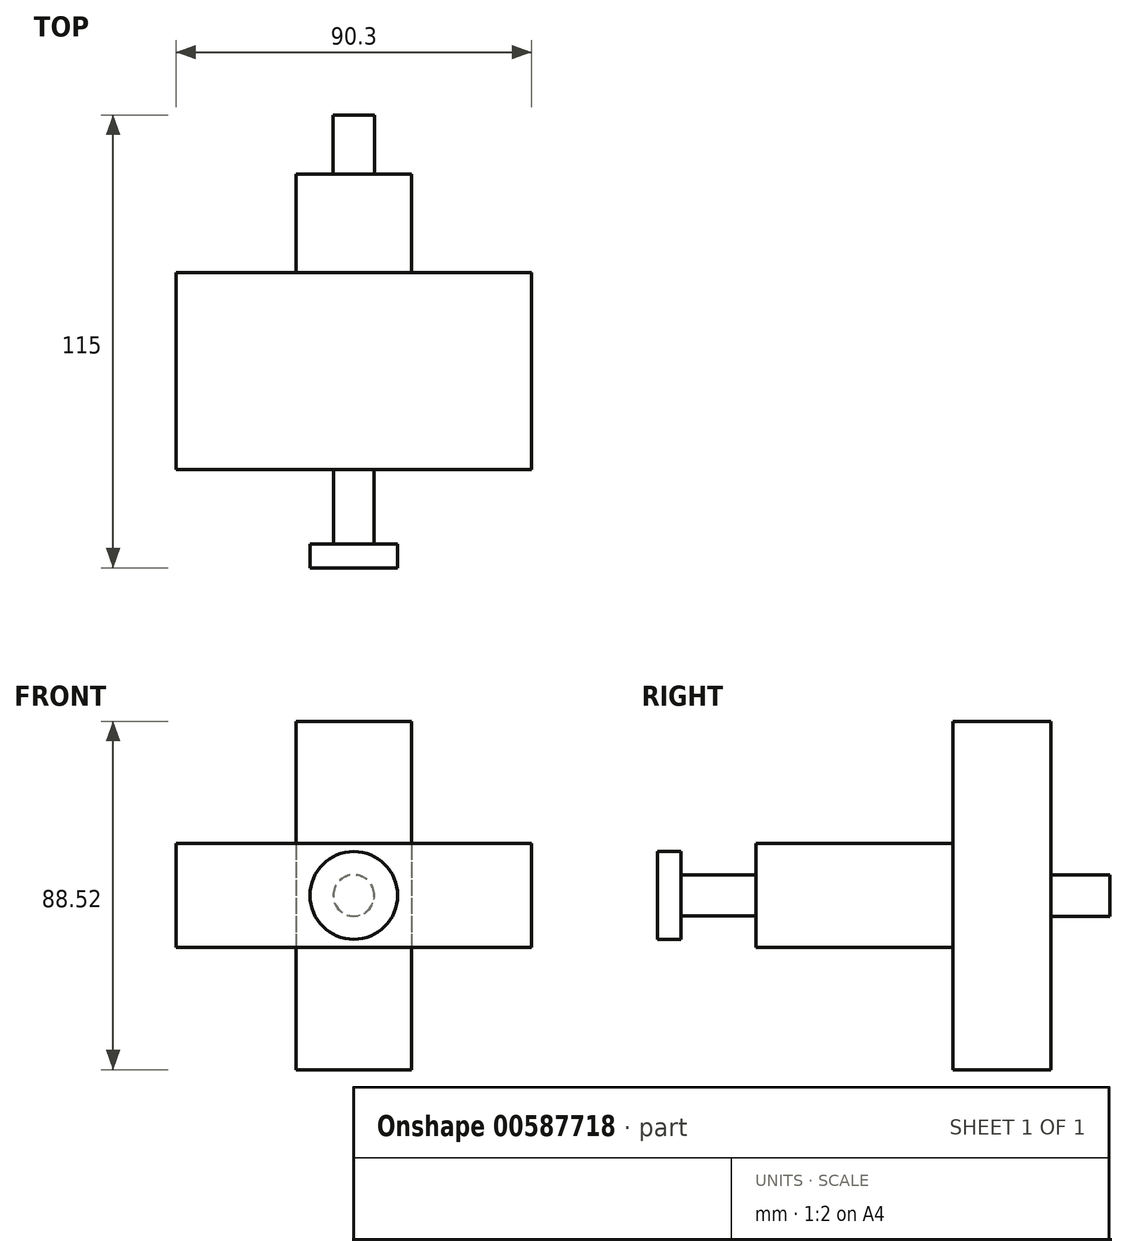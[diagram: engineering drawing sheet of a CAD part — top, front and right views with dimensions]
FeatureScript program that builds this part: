
annotation { "Feature Type Name" : "Feature", "Feature Type Description" : "" }
export const myFeature = defineFeature(function(context is Context, id is Id, definition is map)
    precondition{}
    {
        {
            var Q0;
            Q0=qCreatedBy(makeId("Front.planeOp"),FACE);
            var sketch = newSketch(context, id + "F0", { "sketchPlane" : qUnion([Q0])});
            skLineSegment(sketch, "E0.bottom", {"start": v(45.15, 13.17) * mm, "end": v(-45.15, 13.17) * mm});
            skLineSegment(sketch, "E0.top", {"start": v(45.15, -13.17) * mm, "end": v(-45.15, -13.17) * mm});
            skLineSegment(sketch, "E0.left", {"start": v(45.15, 13.17) * mm, "end": v(45.15, -13.17) * mm});
            skLineSegment(sketch, "E0.right", {"start": v(-45.15, 13.17) * mm, "end": v(-45.15, -13.17) * mm});
            skPoint(sketch, "E0.middle", {"position": v(0, 0) * mm});
            skSolve(sketch);
        }
        {
            var Q0;
            Q0 = qSketchRegion(id + "F0", true);
            extrude(context, id + "F1", {"entities" : qUnion([Q0]), "depth" : 50 * mm, "offsetDistance" : 25 * mm});
        }
        {
            var Q0;
            Q0=qCreatedBy(makeId("Front.planeOp"),FACE);
            var sketch = newSketch(context, id + "F2", { "sketchPlane" : qUnion([Q0])});
            skLineSegment(sketch, "E1.bottom", {"start": v(-14.65, 44.26) * mm, "end": v(14.65, 44.26) * mm});
            skLineSegment(sketch, "E1.top", {"start": v(-14.65, -44.26) * mm, "end": v(14.65, -44.26) * mm});
            skLineSegment(sketch, "E1.left", {"start": v(-14.65, 44.26) * mm, "end": v(-14.65, -44.26) * mm});
            skLineSegment(sketch, "E1.right", {"start": v(14.65, 44.26) * mm, "end": v(14.65, -44.26) * mm});
            skPoint(sketch, "E1.middle", {"position": v(0, 0) * mm});
            skSolve(sketch);
        }
        {
            var Q0;
            Q0 = qSketchRegion(id + "F2", true);
            extrude(context, id + "F3", {"entities" : qUnion([Q0]), "operationType" : NewBodyOperationType.ADD, "depth" : -25 * mm, "offsetDistance" : 25 * mm});
        }
        {
            var Q0;
            Q0=qCreatedBy(makeId("Front.planeOp"),FACE);
            var sketch = newSketch(context, id + "F4", { "sketchPlane" : qUnion([Q0])});
            skCircle(sketch, "E2", {"center": v(0, 0) * mm, "radius": 8.47 * mm});
            skSolve(sketch);
        }
        {
            var Q0;
            Q0 = qSketchRegion(id + "F4", true);
            extrude(context, id + "F5", {"entities" : qUnion([Q0]), "operationType" : NewBodyOperationType.ADD, "depth" : 25 * mm, "offsetDistance" : 25 * mm});
        }
        {
            var Q0;
            Q0=qCreatedBy(makeId("Front.planeOp"),FACE);
            var sketch = newSketch(context, id + "F6", { "sketchPlane" : qUnion([Q0])});
            skCircle(sketch, "E3", {"center": v(0, 0) * mm, "radius": 5.18 * mm});
            skSolve(sketch);
        }
        {
            var Q0;
            Q0 = qSketchRegion(id + "F6", true);
            extrude(context, id + "F7", {"entities" : qUnion([Q0]), "operationType" : NewBodyOperationType.ADD, "depth" : 70 * mm, "offsetDistance" : 25 * mm});
        }
        {
            var Q0;
            Q0=qCreatedBy(makeId("Front.planeOp"),FACE);
            var sketch = newSketch(context, id + "F8", { "sketchPlane" : qUnion([Q0])});
            skCircle(sketch, "E4", {"center": v(0, 0) * mm, "radius": 5.28 * mm});
            skSolve(sketch);
        }
        {
            var Q0;
            Q0 = qSketchRegion(id + "F8", true);
            extrude(context, id + "F9", {"entities" : qUnion([Q0]), "operationType" : NewBodyOperationType.ADD, "depth" : -40 * mm, "offsetDistance" : 25 * mm});
        }
        {
            var Q0;
            Q0=qCreatedBy(makeId("Front.planeOp"),FACE);
            cPlane(context, id + "F10", {"entities" : qUnion([Q0]), "cplaneType" : CPlaneType.OFFSET, "offset" : 50 * mm, "width" : 150 * mm, "height" : 150 * mm});
        }
        {
            var Q0;
            Q0=qCreatedBy(id+"F10.planeOp",FACE);
            cPlane(context, id + "F11", {"entities" : qUnion([Q0]), "cplaneType" : CPlaneType.OFFSET, "offset" : 25 * mm, "width" : 150 * mm, "height" : 150 * mm});
        }
        {
            var Q0;
            Q0=qCreatedBy(id+"F11.planeOp",FACE);
            var sketch = newSketch(context, id + "F12", { "sketchPlane" : qUnion([Q0])});
            skCircle(sketch, "E5", {"center": v(0, 0) * mm, "radius": 11.13 * mm});
            skSolve(sketch);
        }
        {
            var Q0;
            Q0 = qSketchRegion(id + "F12", true);
            extrude(context, id + "F13", {"entities" : qUnion([Q0]), "operationType" : NewBodyOperationType.ADD, "depth" : -6 * mm, "offsetDistance" : 25 * mm});
        }
    });
